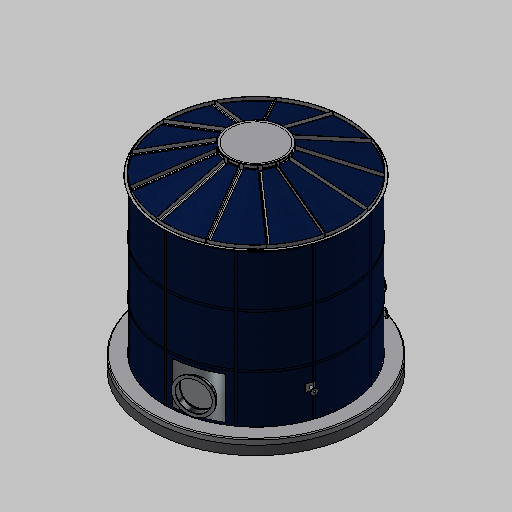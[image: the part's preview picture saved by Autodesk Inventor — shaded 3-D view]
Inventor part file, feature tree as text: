
AUTODESK INVENTOR PART (.ipt)
format: ipt  version: 2025.2 (Build 292293000, 293)  size: 1,589,248 bytes
history: native  units: mm
features: other x33, extrude x15, revolve x2, pattern_linear x2, chamfer x1, pattern_circular x1, projected_geometry x1
ambient origin geometry x7: Origin, YZ Plane, XZ Plane, X Axis, Y Axis, Z Axis, Center Point
bodies: Solid11 (feature_tree), Solid12 (feature_tree)
feature tree (55):
  other  "Concrete Foundation"
  extrude  "Minimal Concrete"  Depth=250.0mm TaperAngle=0.0deg
  extrude  "Concrete Above Level 0.00m "  Depth=8900.0mm
  other  "Bottom L-Profile"
  other  "TankWall"
  extrude  "Extrusion4"  Depth=150.0mm TaperAngle=0.0deg
  revolve  "Revolution6"  [1 undecoded]
  pattern_linear  "Vertical Bolt spots"  Spacing1=7.0mm  [1 undecoded]
  pattern_linear  "Horizontal Bolt Spots"  Count1=900  [1 undecoded]
  other  "Top L-Profile"
  other  "Concrete Base"
  chamfer  "Concrete Base Chamfer"  Angle=90.0deg  [1 undecoded]
  other  "Manhole Elevation Plane"
  other  "Manhole Sketch"
  extrude  "Manhole Plate"  Depth=4.0mm
  other  "Manhole FLange"
  extrude  "ManholeHole"  Depth=10.0mm
  other  "Nozzle1 Elevation Plane"
  extrude  "Nozzle1  Plate"  Depth=7250.0mm
  other  "Nozzle1 Flange"
  extrude  "Nozzle1 Hole"  TaperAngle=90.0deg  [1 undecoded]
  other  "Roof edge L-Profile"
  other  "Roof Ring"
  other  "Roof Rib"
  extrude  "Roof Connection Plate"  Depth=15.0mm
  extrude  "Roof L-Profile"  TaperAngle=90.0deg  [1 undecoded]
  extrude  "Roof L-Profile2"  Depth=60.0mm
  pattern_circular  "Roof Connection Plate Pattern"  [2 undecoded]
  revolve  "Revolution16"  [1 undecoded]
  extrude  "Roofplate"  Depth=60.0mm
  other  "Nozzle2 Elevation Plane"
  other  "Nozzle3 Elevation Plane"
  other  "Nozzle4 Elevation Plane"
  other  "Nozzle5 Elevation Plane"
  other  "Nozzle6 Elevation Plane"
  other  "Nozzle7 Elevation Plane"
  other  "Nozzle8 Elevation Plane"
  other  "Nozzle2 Sketch"
  extrude  "Nozzle2  Plate"  Depth=1450.0mm
  other  "Nozzle2 Flange"
  extrude  "Nozzle2 Hole"  TaperAngle=90.0deg  [1 undecoded]
  other  "Nozzle3 Sketch"
  extrude  "Nozzle3  Plate"  Depth=1571.0mm
  other  "Nozzle3 Flange"
  extrude  "Nozzle3 Hole"  Depth=1440.0mm
  other  "Level 0.00"
  other  "Bottom L-Profile 70x70x7"
  other  "Tank Wall"
  other  "Top L-Profile 70x70x7"
  projected_geometry  "Projected Loop2"
  other  "ManHole"
  other  "ConcreteBase"
  other  "Nozzle1"
  other  "Roof"
  other  "Nozzle1 Sketch"
note: 10 required parameter values undecoded (feature->parameter linkage not recoverable at this tier; creation-order binding heuristic only, values carry confidence <= 0.55)